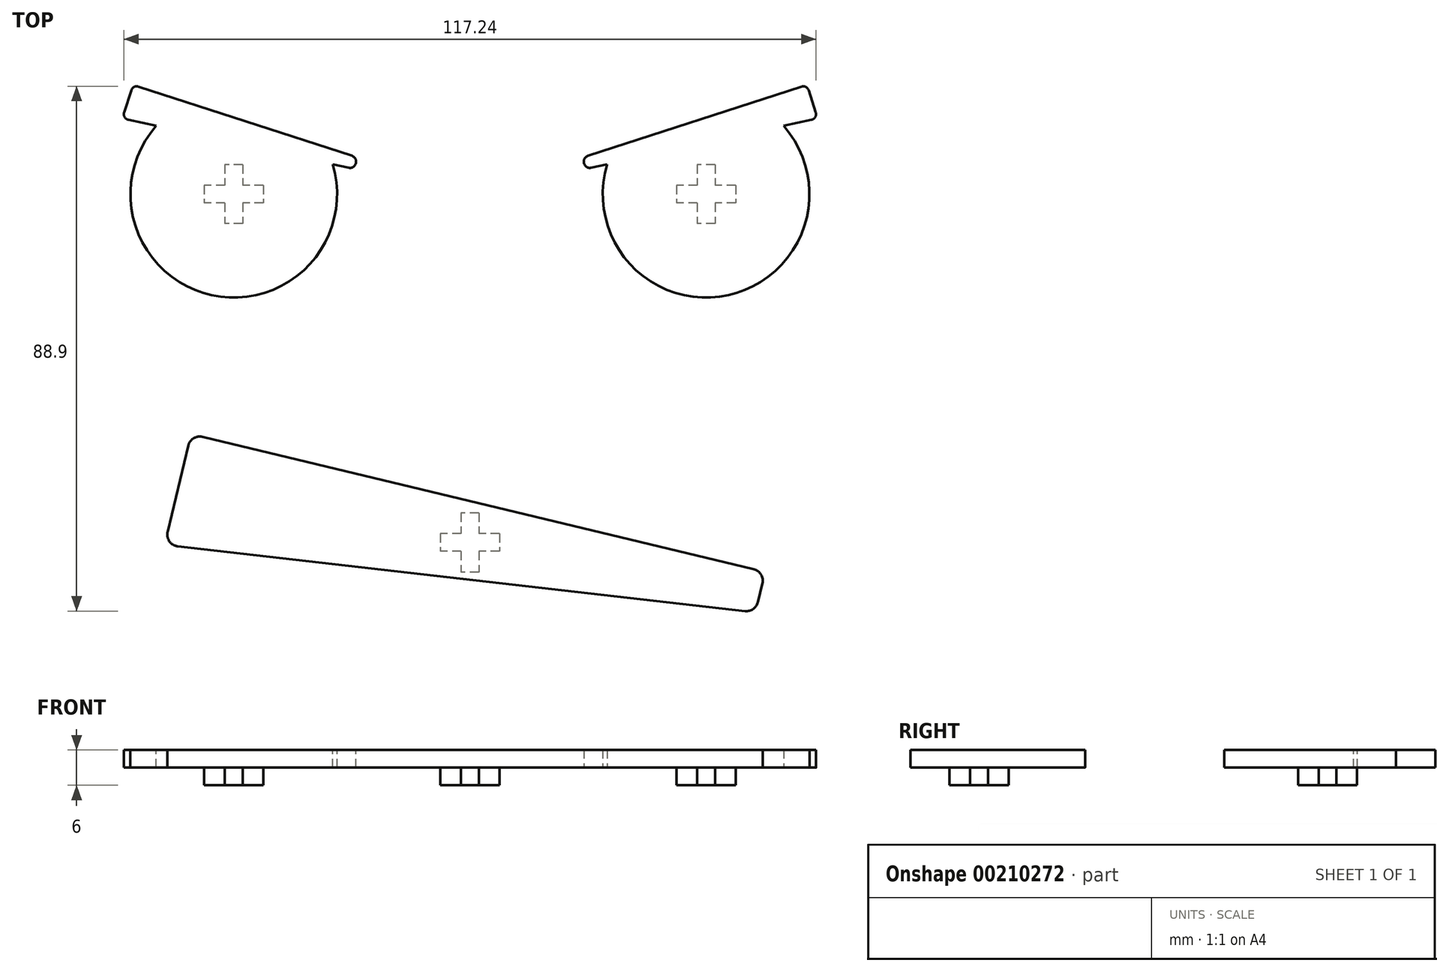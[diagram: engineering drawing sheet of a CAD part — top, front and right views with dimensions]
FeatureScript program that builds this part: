
annotation { "Feature Type Name" : "Feature", "Feature Type Description" : "" }
export const myFeature = defineFeature(function(context is Context, id is Id, definition is map)
    precondition{}
    {
        {
            var Q0;
            Q0=qCreatedBy(makeId("Top.planeOp"),FACE);
            var sketch = newSketch(context, id + "F0", { "sketchPlane" : qUnion([Q0])});
            skArc(sketch, "E0", {"start": v(-16.75, 5.06) * mm, "mid": v(3.72, -17.1) * mm, "end": v(13.13, 11.57) * mm});
            skLineSegment(sketch, "E1", {"start": v(-40, 0) * mm, "end": v(7.96, 15.58) * mm, "construction": true});
            skLineSegment(sketch, "E2", {"start": v(-20.03, 6.49) * mm, "end": v(16.11, 18.23) * mm});
            skLineSegment(sketch, "E3", {"start": v(17.37, 17.59) * mm, "end": v(18.58, 13.89) * mm});
            skLineSegment(sketch, "E4", {"start": v(17.84, 12.6) * mm, "end": v(13.13, 11.57) * mm});
            skLineSegment(sketch, "E5", {"start": v(-20.64, 5.14) * mm, "end": v(-20.67, 5.23) * mm});
            skPoint(sketch, "E6.visualSharp", {"position": v(17.06, 18.54) * mm});
            skArc(sketch, "E6.filletArc", {"start": v(17.37, 17.59) * mm, "mid": v(16.88, 18.17) * mm, "end": v(16.11, 18.23) * mm});
            skPoint(sketch, "E7.visualSharp", {"position": v(18.92, 12.83) * mm});
            skArc(sketch, "E7.filletArc", {"start": v(17.84, 12.6) * mm, "mid": v(18.5, 13.08) * mm, "end": v(18.58, 13.89) * mm});
            skPoint(sketch, "E8.visualSharp", {"position": v(-20.36, 4.28) * mm});
            skArc(sketch, "E8.filletArc", {"start": v(-20.64, 5.14) * mm, "mid": v(-20.19, 4.58) * mm, "end": v(-19.48, 4.47) * mm});
            skPoint(sketch, "E9.visualSharp", {"position": v(-20.98, 6.18) * mm});
            skArc(sketch, "E9.filletArc", {"start": v(-20.03, 6.49) * mm, "mid": v(-20.6, 6) * mm, "end": v(-20.67, 5.23) * mm});
            skLineSegment(sketch, "E10.trimOffspring", {"start": v(-16.75, 5.06) * mm, "end": v(-19.48, 4.47) * mm});
            skLineSegment(sketch, "E11", {"start": v(0, 0) * mm, "end": v(-40, 0) * mm, "construction": true});
            skLineSegment(sketch, "E12", {"start": v(-40, -79.02) * mm, "end": v(-40, 28.03) * mm, "construction": true});
            skLineSegment(sketch, "E13", {"start": v(-85.29, -41.1) * mm, "end": v(8.06, -63.53) * mm});
            skLineSegment(sketch, "E14", {"start": v(9.53, -65.94) * mm, "end": v(8.78, -69.09) * mm});
            skLineSegment(sketch, "E15", {"start": v(6.6, -70.6) * mm, "end": v(-89.5, -59.63) * mm});
            skLineSegment(sketch, "E16", {"start": v(-87.7, -42.58) * mm, "end": v(-91.2, -57.18) * mm});
            skLineSegment(sketch, "E17", {"start": v(9.18, -67.4) * mm, "end": v(-89.48, -50) * mm, "construction": true});
            skPoint(sketch, "E18.visualSharp", {"position": v(10, -64) * mm});
            skArc(sketch, "E18.filletArc", {"start": v(9.53, -65.94) * mm, "mid": v(9.3, -64.43) * mm, "end": v(8.06, -63.53) * mm});
            skPoint(sketch, "E19.visualSharp", {"position": v(8.36, -70.8) * mm});
            skArc(sketch, "E19.filletArc", {"start": v(6.6, -70.6) * mm, "mid": v(7.98, -70.26) * mm, "end": v(8.78, -69.09) * mm});
            skPoint(sketch, "E20.visualSharp", {"position": v(-91.74, -59.38) * mm});
            skArc(sketch, "E20.filletArc", {"start": v(-91.2, -57.18) * mm, "mid": v(-90.9, -58.8) * mm, "end": v(-89.5, -59.63) * mm});
            skPoint(sketch, "E21.visualSharp", {"position": v(-87.23, -40.63) * mm});
            skArc(sketch, "E21.filletArc", {"start": v(-85.29, -41.1) * mm, "mid": v(-86.8, -41.34) * mm, "end": v(-87.7, -42.58) * mm});
            skSolve(sketch);
        }
        {
            var Q0;
            Q0=qSketchRegion(id+"F0",true);
            extrude(context, id + "F1", {"entities" : qUnion([Q0]), "depth" : 3 * mm});
        }
        {
            var Q0;
            Q0=qSketchRegion(id+"F0",true);
            extrude(context, id + "F2", {"entities" : qUnion([Q0]), "depth" : 3 * mm});
        }
        {
            var Q0;
            Q0=makeQuery(id+"F1.opExtrude","SWEPT_BODY",BODY,{"disambiguationData":[OSD([sQuery(id+"F0.wireOp",EDGE,"E0"),sQuery(id+"F0.wireOp",EDGE,"E2"),sQuery(id+"F0.wireOp",EDGE,"E3"),sQuery(id+"F0.wireOp",EDGE,"E4"),sQuery(id+"F0.wireOp",EDGE,"E5"),sQuery(id+"F0.wireOp",EDGE,"E6.filletArc"),sQuery(id+"F0.wireOp",EDGE,"E7.filletArc"),sQuery(id+"F0.wireOp",EDGE,"E8.filletArc"),sQuery(id+"F0.wireOp",EDGE,"E9.filletArc"),sQuery(id+"F0.wireOp",EDGE,"E10.trimOffspring")])]});
            var Q1;
            Q1=sQuery(id+"F0.wireOp",EDGE,"E12");
            transform(context, id + "F3", {"entities" : qUnion([Q0]), "transformType" : TransformType.ROTATION, "transformAxis" : qUnion([Q1]), "angle" : 180 * degree, "makeCopy" : true});
        }
        {
            var Q0;
            Q0=makeQuery(id+"F3.opPattern","COPY",BODY,{"derivedFrom":makeQuery(id+"F1.opExtrude","SWEPT_BODY",BODY,{"disambiguationData":[OSD([sQuery(id+"F0.wireOp",EDGE,"E0"),sQuery(id+"F0.wireOp",EDGE,"E2"),sQuery(id+"F0.wireOp",EDGE,"E3"),sQuery(id+"F0.wireOp",EDGE,"E4"),sQuery(id+"F0.wireOp",EDGE,"E5"),sQuery(id+"F0.wireOp",EDGE,"E6.filletArc"),sQuery(id+"F0.wireOp",EDGE,"E7.filletArc"),sQuery(id+"F0.wireOp",EDGE,"E8.filletArc"),sQuery(id+"F0.wireOp",EDGE,"E9.filletArc"),sQuery(id+"F0.wireOp",EDGE,"E10.trimOffspring")])]}),"instanceName":"1"});
            var Q1;
            Q1=qCreatedBy(makeId("Top.planeOp"),FACE);
            transform(context, id + "F4", {"entities" : qUnion([Q0]), "transformType" : TransformType.TRANSLATION_DISTANCE, "transformDirection" : qUnion([Q1]), "distance" : 3 * mm, "makeCopy" : false});
        }
        {
            var Q0;
            Q0=makeQuery(id+"F1.opExtrude","CAP_FACE",FACE,{"disambiguationData":[OSD([sQuery(id+"F0.wireOp",EDGE,"E0"),sQuery(id+"F0.wireOp",EDGE,"E2"),sQuery(id+"F0.wireOp",EDGE,"E3"),sQuery(id+"F0.wireOp",EDGE,"E4"),sQuery(id+"F0.wireOp",EDGE,"E5"),sQuery(id+"F0.wireOp",EDGE,"E6.filletArc"),sQuery(id+"F0.wireOp",EDGE,"E7.filletArc"),sQuery(id+"F0.wireOp",EDGE,"E8.filletArc"),sQuery(id+"F0.wireOp",EDGE,"E9.filletArc"),sQuery(id+"F0.wireOp",EDGE,"E10.trimOffspring")])],"isStart":true});
            var sketch = newSketch(context, id + "F5", { "sketchPlane" : qUnion([Q0])});
            skPoint(sketch, "E22", {"position": v(0, 0) * mm});
            skLineSegment(sketch, "E23.bottom", {"start": v(1.5, -5) * mm, "end": v(-1.5, -5) * mm});
            skLineSegment(sketch, "E23.top", {"start": v(1.5, 5) * mm, "end": v(-1.5, 5) * mm});
            skLineSegment(sketch, "E23.left", {"start": v(1.5, -5) * mm, "end": v(1.5, 5) * mm});
            skLineSegment(sketch, "E23.right", {"start": v(-1.5, -5) * mm, "end": v(-1.5, 5) * mm});
            skLineSegment(sketch, "E24.bottom", {"start": v(5, -1.5) * mm, "end": v(-5, -1.5) * mm});
            skLineSegment(sketch, "E24.top", {"start": v(5, 1.5) * mm, "end": v(-5, 1.5) * mm});
            skLineSegment(sketch, "E24.left", {"start": v(5, -1.5) * mm, "end": v(5, 1.5) * mm});
            skLineSegment(sketch, "E24.right", {"start": v(-5, -1.5) * mm, "end": v(-5, 1.5) * mm});
            skLineSegment(sketch, "E25", {"start": v(0, 0) * mm, "end": v(5, 0) * mm, "construction": true});
            skLineSegment(sketch, "E26", {"start": v(0, -5) * mm, "end": v(0, 0) * mm, "construction": true});
            skLineSegment(sketch, "E27.1.0.0", {"start": v(-78.5, -5) * mm, "end": v(-81.5, -5) * mm});
            skLineSegment(sketch, "E27.1.0.1", {"start": v(-81.5, -5) * mm, "end": v(-81.5, 5) * mm});
            skLineSegment(sketch, "E27.1.0.2", {"start": v(-75, -1.5) * mm, "end": v(-85, -1.5) * mm});
            skLineSegment(sketch, "E27.1.0.3", {"start": v(-85, -1.5) * mm, "end": v(-85, 1.5) * mm});
            skLineSegment(sketch, "E27.1.0.4", {"start": v(-75, 1.5) * mm, "end": v(-85, 1.5) * mm});
            skLineSegment(sketch, "E27.1.0.5", {"start": v(-78.5, 5) * mm, "end": v(-81.5, 5) * mm});
            skLineSegment(sketch, "E27.1.0.6", {"start": v(-78.5, -5) * mm, "end": v(-78.5, 5) * mm});
            skLineSegment(sketch, "E27.1.0.7", {"start": v(-75, -1.5) * mm, "end": v(-75, 1.5) * mm});
            skLineSegment(sketch, "E27.direction1", {"start": v(-1.5, -5) * mm, "end": v(-81.5, -5) * mm, "construction": true});
            skLineSegment(sketch, "E28.bottom", {"start": v(-38.5, 54) * mm, "end": v(-41.5, 54) * mm});
            skLineSegment(sketch, "E28.top", {"start": v(-38.5, 64) * mm, "end": v(-41.5, 64) * mm});
            skLineSegment(sketch, "E28.left", {"start": v(-38.5, 54) * mm, "end": v(-38.5, 64) * mm});
            skLineSegment(sketch, "E28.right", {"start": v(-41.5, 54) * mm, "end": v(-41.5, 64) * mm});
            skLineSegment(sketch, "E29.bottom", {"start": v(-35, 57.5) * mm, "end": v(-45, 57.5) * mm});
            skLineSegment(sketch, "E29.top", {"start": v(-35, 60.5) * mm, "end": v(-45, 60.5) * mm});
            skLineSegment(sketch, "E29.left", {"start": v(-35, 57.5) * mm, "end": v(-35, 60.5) * mm});
            skLineSegment(sketch, "E29.right", {"start": v(-45, 57.5) * mm, "end": v(-45, 60.5) * mm});
            skLineSegment(sketch, "E30", {"start": v(-45, 59) * mm, "end": v(-35, 59) * mm, "construction": true});
            skLineSegment(sketch, "E31", {"start": v(-40, 54) * mm, "end": v(-40, 64) * mm, "construction": true});
            skSolve(sketch);
        }
        {
            var Q0;
            Q0=qSketchRegion(id+"F5",true);
            extrude(context, id + "F6", {"entities" : qUnion([Q0]), "operationType" : NewBodyOperationType.ADD, "depth" : 3 * mm});
        }
    });
